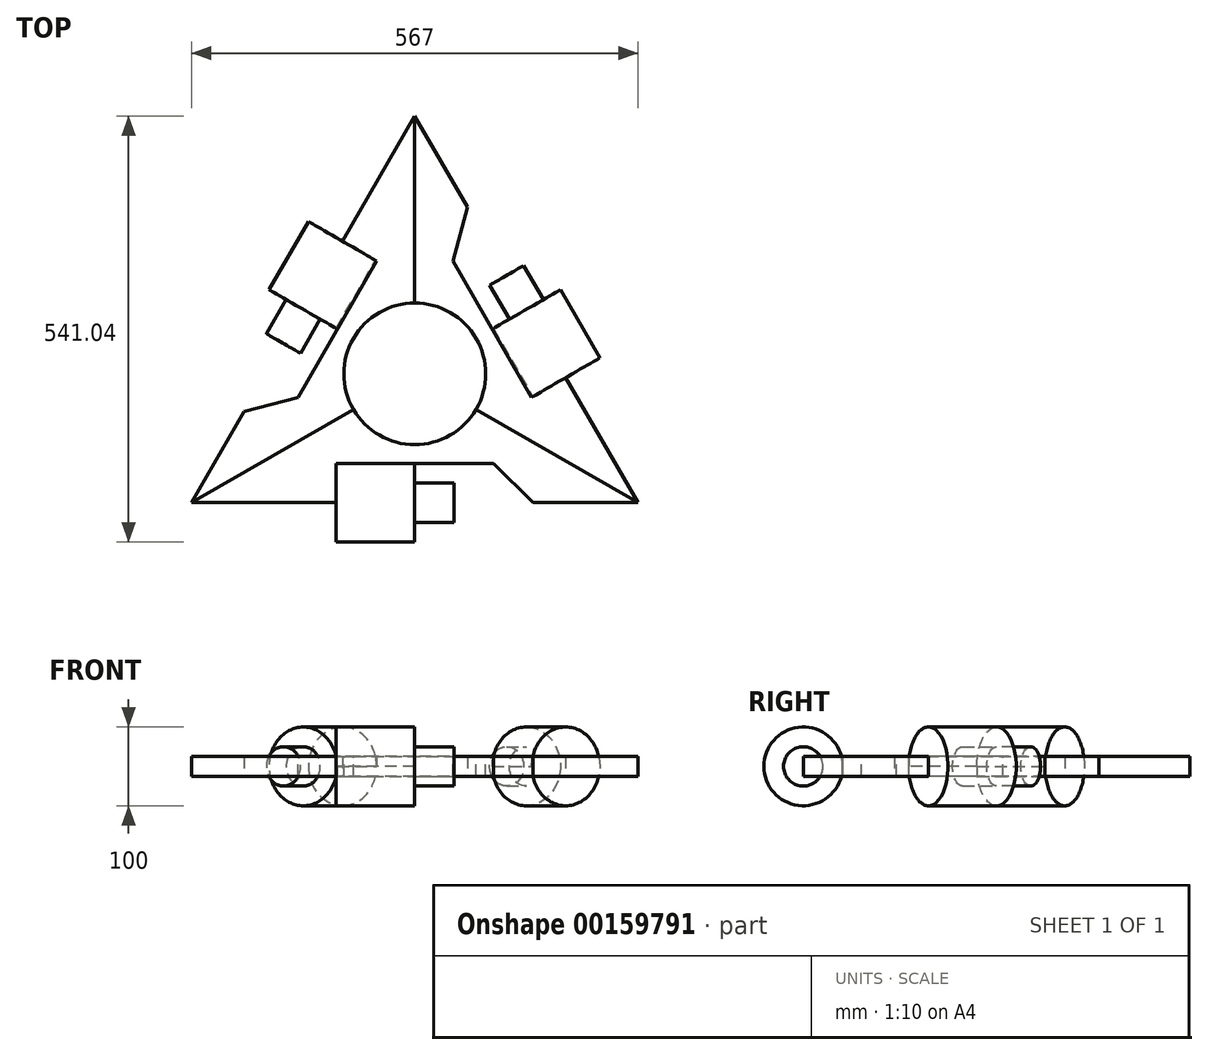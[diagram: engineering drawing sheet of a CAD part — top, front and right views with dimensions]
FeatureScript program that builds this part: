
annotation { "Feature Type Name" : "Feature", "Feature Type Description" : "" }
export const myFeature = defineFeature(function(context is Context, id is Id, definition is map)
    precondition{}
    {
        {
            var Q0;
            Q0=qCreatedBy(makeId("Top.planeOp"),FACE);
            var sketch = newSketch(context, id + "F0", { "sketchPlane" : qUnion([Q0])});
            skLineSegment(sketch, "E0", {"start": v(0, 0) * mm, "end": v(567, 0) * mm});
            skLineSegment(sketch, "E1", {"start": v(0, 0) * mm, "end": v(283.5, 491.04) * mm});
            skLineSegment(sketch, "E2", {"start": v(283.5, 491.04) * mm, "end": v(567, 0) * mm});
            skSolve(sketch);
        }
        {
            var Q0;
            Q0=makeQuery(id+"F0.imprint","IMPRINT",FACE,{"disambiguationData":[TD([[makeQuery(id+"F0.imprint","IMPRINT",EDGE,{"derivedFrom":sQuery(id+"F0.wireOp",EDGE,"E0")}),1.0]])]});
            extrude(context, id + "F1", {"entities" : qUnion([Q0]), "depth" : 25 * mm});
        }
        {
            var Q0;
            Q0=makeQuery(id+"F1.opExtrude","SWEPT_FACE",FACE,{"disambiguationData":[OSD([sQuery(id+"F0.wireOp",EDGE,"E0")])]});
            var sketch = newSketch(context, id + "F2", { "sketchPlane" : qUnion([Q0])});
            skLineSegment(sketch, "E3", {"start": v(0, 0) * mm, "end": v(567, 0) * mm});
            skLineSegment(sketch, "E4", {"start": v(283.5, 0) * mm, "end": v(283.5, 25) * mm});
            skLineSegment(sketch, "E5", {"start": v(283.5, 25) * mm, "end": v(383.5, 25) * mm});
            skLineSegment(sketch, "E6", {"start": v(383.5, 25) * mm, "end": v(383.5, 0) * mm});
            skLineSegment(sketch, "E7", {"start": v(383.5, 0) * mm, "end": v(283.5, 0) * mm});
            skLineSegment(sketch, "E8.bottom", {"start": v(283.5, 25) * mm, "end": v(183.5, 25) * mm});
            skLineSegment(sketch, "E8.top", {"start": v(283.5, 0) * mm, "end": v(183.5, 0) * mm});
            skLineSegment(sketch, "E8.left", {"start": v(283.5, 25) * mm, "end": v(283.5, 0) * mm});
            skLineSegment(sketch, "E8.right", {"start": v(183.5, 25) * mm, "end": v(183.5, 0) * mm});
            skSolve(sketch);
        }
        {
            var Q0;
            Q0=qSketchRegion(id+"F2",true);
            extrude(context, id + "F3", {"entities" : qUnion([Q0]), "operationType" : NewBodyOperationType.REMOVE, "oppositeDirection" : true, "depth" : 50 * mm});
        }
        {
            var Q0;
            Q0=makeQuery(id+"F3.boolean.opBoolean","COPY",FACE,{"derivedFrom":makeQuery(id+"F3.opExtrude","SWEPT_FACE",FACE,{"disambiguationData":[OSD([sQuery(id+"F2.wireOp",EDGE,"E8.right")])]})});
            var sketch = newSketch(context, id + "F4", { "sketchPlane" : qUnion([Q0])});
            skLineSegment(sketch, "E9", {"start": v(0, 0) * mm, "end": v(50, 0) * mm});
            skLineSegment(sketch, "E10", {"start": v(50, 0) * mm, "end": v(50, 25) * mm});
            skLineSegment(sketch, "E11", {"start": v(50, 12.5) * mm, "end": v(0, 12.5) * mm});
            skCircle(sketch, "E12", {"center": v(0, 12.5) * mm, "radius": 50 * mm});
            skSolve(sketch);
        }
        {
            var Q0;
            Q0=qSketchRegion(id+"F4",true);
            var Q1;
            {var subQ0=sQuery(id+"F2.wireOp",EDGE,"E8.right");var subQ1=makeQuery(id+"F3.boolean.opBoolean","COPY",EDGE,{"derivedFrom":makeQuery(id+"F3.opExtrude","CAP_EDGE",EDGE,{"disambiguationData":[OSD([subQ0])],"isStart":true})});var subQ7=sQuery(id+"F4.wireOp",EDGE,"E9");var subQ9=makeQuery(id+"F4.imprint","INTERSECT",VERTEX,{"derivedFrom":[subQ1,subQ7]});Q1=makeQuery(id+"F4.imprint","IMPRINT",FACE,{"disambiguationData":[TD([[makeQuery(id+"F4.imprint","IMPRINT",EDGE,{"disambiguationData":[TD([[subQ9,1.0]])],"derivedFrom":subQ7}),1.0]])]});}
            extrude(context, id + "F5", {"entities" : qUnion([Q0, Q1]), "operationType" : NewBodyOperationType.ADD, "depth" : 100 * mm});
        }
        {
            var Q0;
            Q0=makeQuery(id+"F5.opExtrude","CAP_FACE",FACE,{"disambiguationData":[OSD([sQuery(id+"F4.wireOp",EDGE,"E9"),sQuery(id+"F4.wireOp",EDGE,"E10"),sQuery(id+"F4.wireOp",EDGE,"E12")])],"isStart":false});
            var sketch = newSketch(context, id + "F6", { "sketchPlane" : qUnion([Q0])});
            skCircle(sketch, "E13", {"center": v(0, 12.5) * mm, "radius": 25 * mm});
            skSolve(sketch);
        }
        {
            var Q0;
            Q0=qSketchRegion(id+"F6",true);
            extrude(context, id + "F7", {"entities" : qUnion([Q0]), "operationType" : NewBodyOperationType.ADD, "depth" : 50 * mm});
        }
        {
            var Q0;
            Q0=makeQuery(id+"F3.boolean.opBoolean","COPY",FACE,{"derivedFrom":makeQuery(id+"F3.opExtrude","SWEPT_FACE",FACE,{"disambiguationData":[OSD([sQuery(id+"F2.wireOp",EDGE,"E6")])]})});
            extrude(context, id + "F8", {"entities" : qUnion([Q0]), "operationType" : NewBodyOperationType.REMOVE, "oppositeDirection" : true, "depth" : 50 * mm});
        }
        {
            var Q0;
            {var subQ0=sQuery(id+"F2.wireOp",EDGE,"E6");Q0=makeQuery(id+"F8.boolean.opBoolean","COPY",EDGE,{"derivedFrom":makeQuery(id+"F8.opExtrude","CAP_EDGE",EDGE,{"disambiguationData":[OSD([subQ0]),TDD([makeQuery(id+"F3.boolean.opBoolean","COPY",EDGE,{"derivedFrom":makeQuery(id+"F3.opExtrude","CAP_EDGE",EDGE,{"disambiguationData":[OSD([subQ0])],"isStart":true})})])],"isStart":false})});}
            chamfer(context, id + "F9", {"entities" : qUnion([Q0]), "width" : 50 * mm, "tangentPropagation" : true});
        }
        {
            var Q0;
            Q0=makeQuery(id+"F1.opExtrude","CAP_FACE",FACE,{"disambiguationData":[OSD([sQuery(id+"F0.wireOp",EDGE,"E0"),sQuery(id+"F0.wireOp",EDGE,"E1"),sQuery(id+"F0.wireOp",EDGE,"E2")])],"isStart":false});
            var sketch = newSketch(context, id + "F10", { "sketchPlane" : qUnion([Q0])});
            skLineSegment(sketch, "E14", {"start": v(567, 0) * mm, "end": v(141.75, 245.52) * mm});
            skLineSegment(sketch, "E15", {"start": v(0, 0) * mm, "end": v(425.25, 245.52) * mm});
            skCircle(sketch, "E16", {"center": v(283.5, 163.68) * mm, "radius": 90 * mm});
            skSolve(sketch);
        }
        {
            var Q0;
            Q0=qSketchRegion(id+"F10",true);
            var Q1;
            {var subQ1=makeQuery(id+"F1.opExtrude","CAP_EDGE",EDGE,{"disambiguationData":[OSD([sQuery(id+"F0.wireOp",EDGE,"E1")])],"isStart":false});var subQ3=sQuery(id+"F10.wireOp",EDGE,"E14");var subQ4=makeQuery(id+"F10.imprint","INTERSECT",VERTEX,{"derivedFrom":[subQ1,subQ3]});Q1=makeQuery(id+"F10.imprint","IMPRINT",FACE,{"disambiguationData":[TD([[makeQuery(id+"F10.imprint","IMPRINT",EDGE,{"disambiguationData":[TD([[subQ4,1.0]])],"derivedFrom":subQ3}),-1.0]])]});}
            var Q2;
            {var subQ2=sQuery(id+"F0.wireOp",EDGE,"E2");var subQ3=makeQuery(id+"F1.opExtrude","CAP_EDGE",EDGE,{"disambiguationData":[OSD([subQ2])],"isStart":false});var subQ7=sQuery(id+"F10.wireOp",EDGE,"E15");var subQ8=makeQuery(id+"F10.imprint","INTERSECT",VERTEX,{"derivedFrom":[subQ3,subQ7]});Q2=makeQuery(id+"F10.imprint","IMPRINT",FACE,{"disambiguationData":[TD([[makeQuery(id+"F10.imprint","IMPRINT",EDGE,{"disambiguationData":[TD([[subQ8,1.0]])],"derivedFrom":subQ7}),-1.0]])]});}
            var Q3;
            {var subQ0=sQuery(id+"F10.wireOp",EDGE,"E14");var subQ1=sQuery(id+"F0.wireOp",EDGE,"E1");var subQ2=makeQuery(id+"F1.opExtrude","CAP_EDGE",EDGE,{"disambiguationData":[OSD([subQ1])],"isStart":false});var subQ3=makeQuery(id+"F10.imprint","INTERSECT",VERTEX,{"derivedFrom":[subQ2,subQ0]});Q3=makeQuery(id+"F10.imprint","IMPRINT",FACE,{"disambiguationData":[TD([[makeQuery(id+"F10.imprint","IMPRINT",EDGE,{"disambiguationData":[TD([[subQ3,1.0]])],"derivedFrom":subQ0}),1.0]])]});}
            extrude(context, id + "F11", {"entities" : qUnion([Q0, Q1, Q2, Q3]), "operationType" : NewBodyOperationType.REMOVE, "oppositeDirection" : true, "depth" : 25 * mm});
        }
        {
            var Q0;
            Q0=makeQuery(id+"F1.opExtrude","CAP_FACE",FACE,{"disambiguationData":[OSD([sQuery(id+"F0.wireOp",EDGE,"E0"),sQuery(id+"F0.wireOp",EDGE,"E1"),sQuery(id+"F0.wireOp",EDGE,"E2")])],"isStart":false});
            var sketch = newSketch(context, id + "F12", { "sketchPlane" : qUnion([Q0])});
            skLineSegment(sketch, "E17", {"start": v(361.44, 118.68) * mm, "end": v(283.5, 163.68) * mm});
            skLineSegment(sketch, "E18", {"start": v(205.56, 118.68) * mm, "end": v(283.5, 163.68) * mm});
            skSolve(sketch);
        }
        {
            var Q0;
            Q0=qCreatedBy(makeId("Right.planeOp"),FACE);
            var Q1;
            Q1=sQuery(id+"F12.wireOp",VERTEX,"E18.end");
            cPlane(context, id + "F13", {"entities" : qUnion([Q0, Q1]), "cplaneType" : CPlaneType.PLANE_POINT, "offset" : 150 * mm, "width" : 150 * mm, "height" : 150 * mm});
        }
        {
            var Q0;
            Q0=qCreatedBy(id+"F13.planeOp",FACE);
            var sketch = newSketch(context, id + "F14", { "sketchPlane" : qUnion([Q0])});
            skPoint(sketch, "E19.0", {"position": v(163.68, 25) * mm});
            skLineSegment(sketch, "E20", {"start": v(163.68, 25) * mm, "end": v(163.68, -25) * mm});
            skSolve(sketch);
        }
        {
            var Q0;
            Q0=makeQuery(id+"F1.opExtrude","SWEPT_BODY",BODY,{"disambiguationData":[OSD([sQuery(id+"F0.wireOp",EDGE,"E0"),sQuery(id+"F0.wireOp",EDGE,"E1"),sQuery(id+"F0.wireOp",EDGE,"E2")])]});
            var Q1;
            Q1=sQuery(id+"F14.wireOp",EDGE,"E20");
            circularPattern(context, id + "F15", {"entities" : qUnion([Q0]), "axis" : qUnion([Q1]), "angle" : 120 * degree, "instanceCount" : 3});
        }
    });
